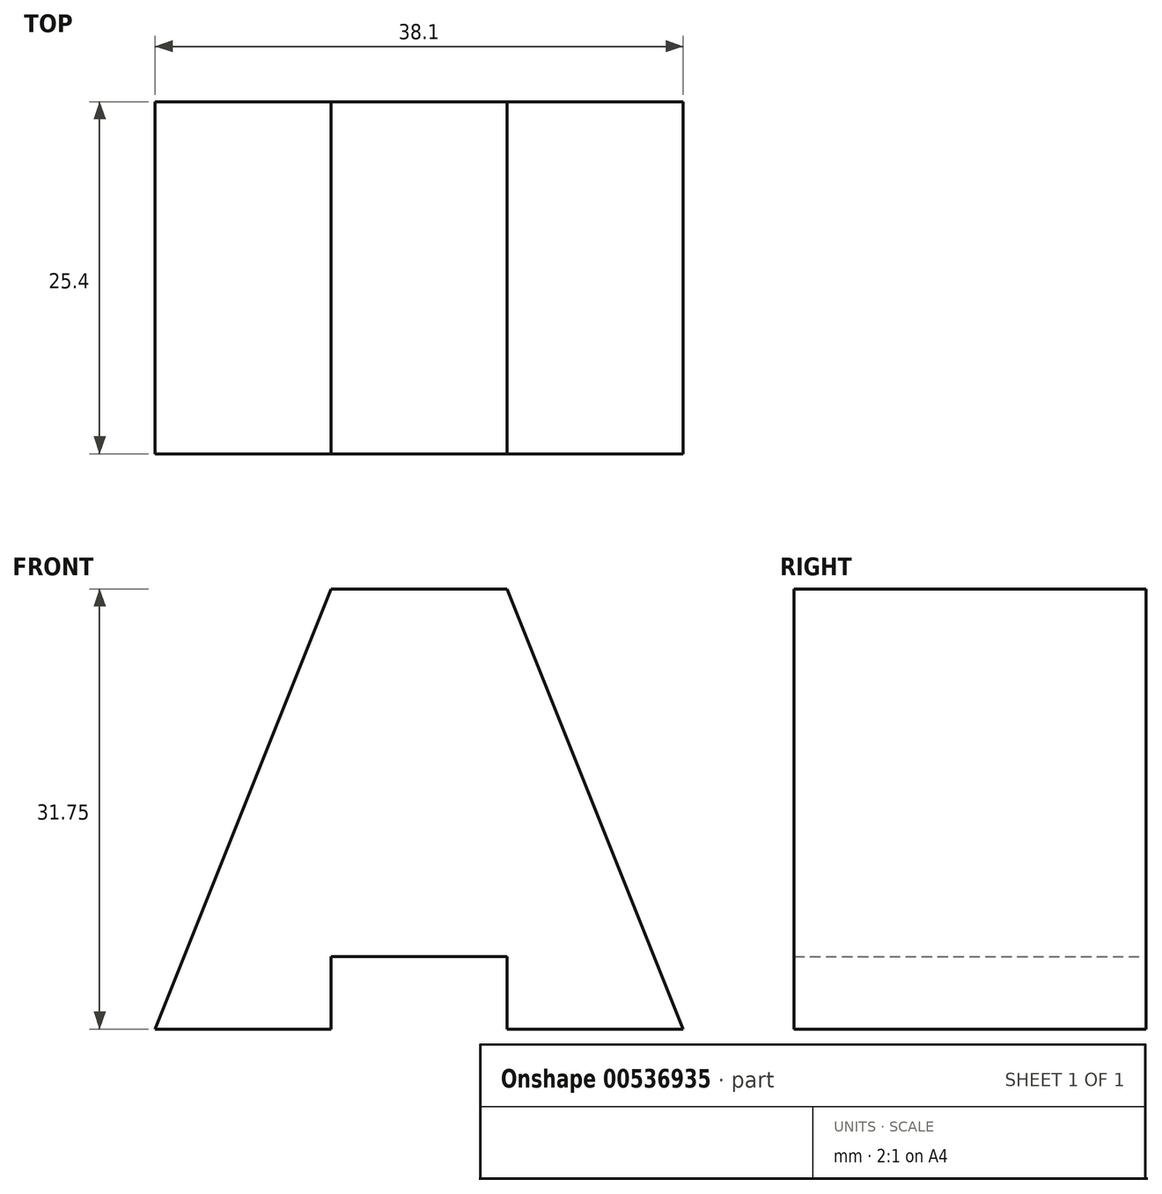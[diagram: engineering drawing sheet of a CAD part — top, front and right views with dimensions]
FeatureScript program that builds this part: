
annotation { "Feature Type Name" : "Feature", "Feature Type Description" : "" }
export const myFeature = defineFeature(function(context is Context, id is Id, definition is map)
    precondition{}
    {
        {
            var Q0;
            Q0=qCreatedBy(makeId("Front.planeOp"),FACE);
            var sketch = newSketch(context, id + "F0", { "sketchPlane" : qUnion([Q0])});
            skLineSegment(sketch, "E0", {"start": v(-38.1, 0) * mm, "end": v(-38.1, 31.75) * mm});
            skLineSegment(sketch, "E1", {"start": v(-38.1, 31.75) * mm, "end": v(0, 31.75) * mm});
            skLineSegment(sketch, "E2", {"start": v(0, 31.75) * mm, "end": v(0, 0) * mm});
            skLineSegment(sketch, "E3", {"start": v(0, 0) * mm, "end": v(-12.7, 0) * mm});
            skLineSegment(sketch, "E4", {"start": v(-12.7, 0) * mm, "end": v(-12.7, 5.22) * mm});
            skLineSegment(sketch, "E5", {"start": v(-12.7, 5.22) * mm, "end": v(-25.4, 5.22) * mm});
            skLineSegment(sketch, "E6", {"start": v(-25.4, 5.22) * mm, "end": v(-25.4, 0) * mm});
            skLineSegment(sketch, "E7", {"start": v(-25.4, 0) * mm, "end": v(-38.1, 0) * mm});
            skSolve(sketch);
        }
        {
            var Q0;
            Q0=makeQuery(id+"F0.imprint","IMPRINT",FACE,{"disambiguationData":[TD([[makeQuery(id+"F0.imprint","IMPRINT",EDGE,{"derivedFrom":sQuery(id+"F0.wireOp",EDGE,"E0")}),-1.0]])]});
            extrude(context, id + "F1", {"entities" : qUnion([Q0]), "depth" : 25.4 * mm, "offsetDistance" : 25.4 * mm});
        }
        {
            var Q0;
            Q0=makeQuery(id+"F1.opExtrude","CAP_FACE",FACE,{"disambiguationData":[OSD([sQuery(id+"F0.wireOp",EDGE,"E0"),sQuery(id+"F0.wireOp",EDGE,"E1"),sQuery(id+"F0.wireOp",EDGE,"E2"),sQuery(id+"F0.wireOp",EDGE,"E3"),sQuery(id+"F0.wireOp",EDGE,"E4"),sQuery(id+"F0.wireOp",EDGE,"E5"),sQuery(id+"F0.wireOp",EDGE,"E6"),sQuery(id+"F0.wireOp",EDGE,"E7")])],"isStart":false});
            var sketch = newSketch(context, id + "F2", { "sketchPlane" : qUnion([Q0])});
            skLineSegment(sketch, "E8", {"start": v(-38.1, 0) * mm, "end": v(-25.4, 31.75) * mm});
            skLineSegment(sketch, "E9", {"start": v(-25.4, 31.75) * mm, "end": v(-12.7, 31.75) * mm});
            skLineSegment(sketch, "E10", {"start": v(-12.7, 31.75) * mm, "end": v(0, 0) * mm});
            skSolve(sketch);
        }
        {
            var Q0;
            {var subQ0=sQuery(id+"F2.wireOp",EDGE,"E8");Q0=makeQuery(id+"F2.imprint","IMPRINT",FACE,{"disambiguationData":[TD([[makeQuery(id+"F2.imprint","IMPRINT",EDGE,{"derivedFrom":subQ0}),1.0]])]});}
            extrude(context, id + "F3", {"entities" : qUnion([Q0]), "operationType" : NewBodyOperationType.REMOVE, "oppositeDirection" : true, "depth" : 25.4 * mm, "offsetDistance" : 25.4 * mm});
        }
        {
            var Q0;
            Q0=makeQuery(id+"F1.opExtrude","CAP_FACE",FACE,{"disambiguationData":[OSD([sQuery(id+"F0.wireOp",EDGE,"E0"),sQuery(id+"F0.wireOp",EDGE,"E1"),sQuery(id+"F0.wireOp",EDGE,"E2"),sQuery(id+"F0.wireOp",EDGE,"E3"),sQuery(id+"F0.wireOp",EDGE,"E4"),sQuery(id+"F0.wireOp",EDGE,"E5"),sQuery(id+"F0.wireOp",EDGE,"E6"),sQuery(id+"F0.wireOp",EDGE,"E7")])],"isStart":false});
            var sketch = newSketch(context, id + "F4", { "sketchPlane" : qUnion([Q0])});
            skLineSegment(sketch, "E11", {"start": v(0, 0) * mm, "end": v(-12.7, 31.75) * mm});
            skSolve(sketch);
        }
        {
            var Q0;
            {var subQ0=sQuery(id+"F4.wireOp",EDGE,"E11");Q0=makeQuery(id+"F4.imprint","IMPRINT",FACE,{"disambiguationData":[TD([[makeQuery(id+"F4.imprint","IMPRINT",EDGE,{"derivedFrom":subQ0}),-1.0]])]});}
            extrude(context, id + "F5", {"entities" : qUnion([Q0]), "operationType" : NewBodyOperationType.REMOVE, "oppositeDirection" : true, "depth" : 25.4 * mm, "offsetDistance" : 25.4 * mm});
        }
    });
